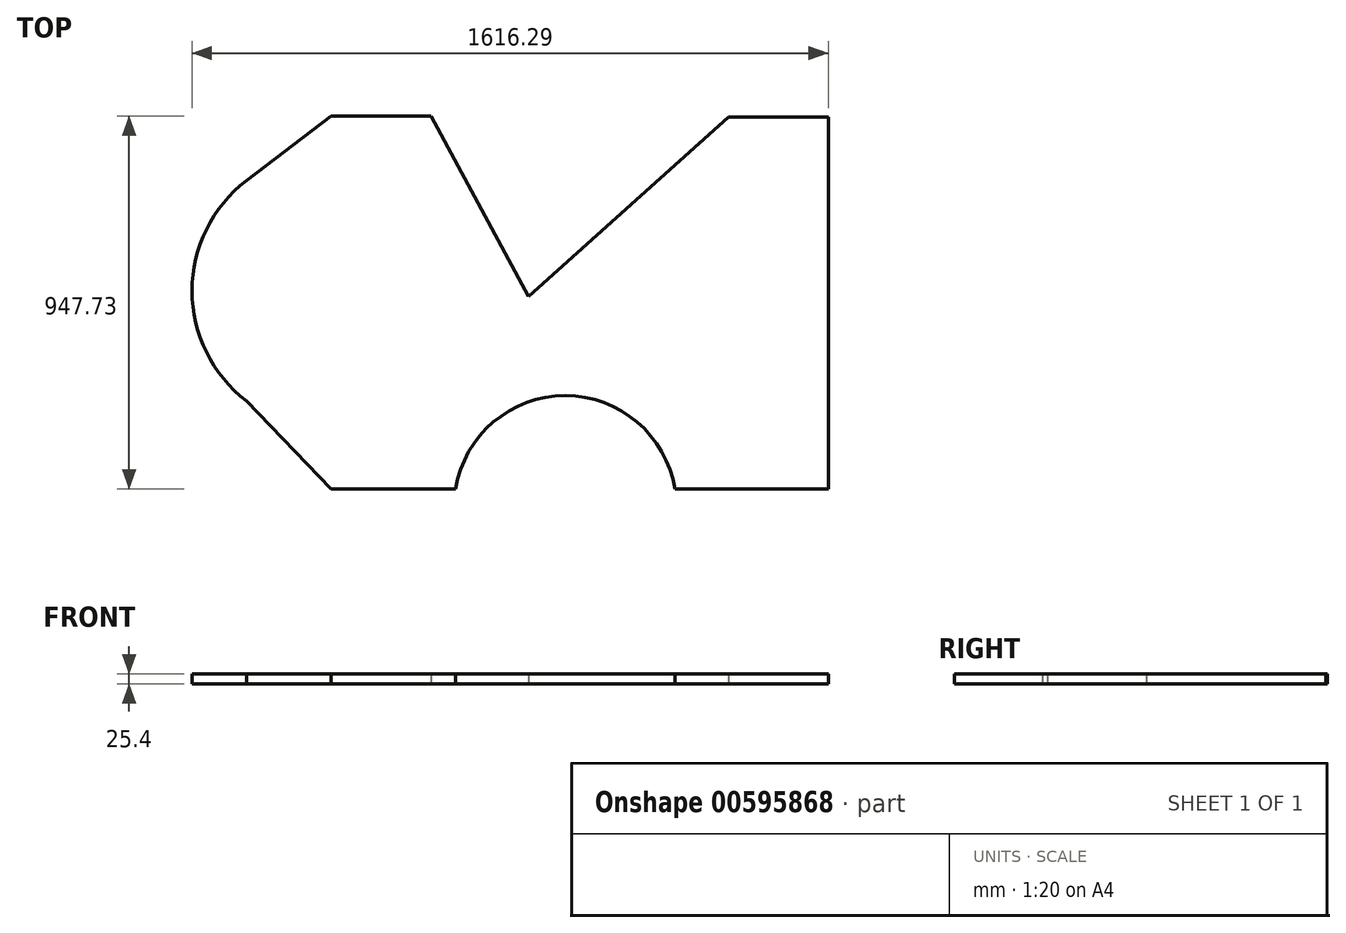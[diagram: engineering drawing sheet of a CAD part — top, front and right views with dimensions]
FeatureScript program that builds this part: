
annotation { "Feature Type Name" : "Feature", "Feature Type Description" : "" }
export const myFeature = defineFeature(function(context is Context, id is Id, definition is map)
    precondition{}
    {
        {
            var Q0;
            Q0=qCreatedBy(makeId("Top.planeOp"),FACE);
            var sketch = newSketch(context, id + "F0", { "sketchPlane" : qUnion([Q0])});
            skLineSegment(sketch, "E0", {"start": v(-501.68, 459.06) * mm, "end": v(-247.68, 459.06) * mm});
            skLineSegment(sketch, "E1", {"start": v(-247.68, 459.06) * mm, "end": v(0, 0) * mm});
            skLineSegment(sketch, "E2", {"start": v(0, 0) * mm, "end": v(508, 455.6) * mm});
            skLineSegment(sketch, "E3", {"start": v(508, 455.6) * mm, "end": v(762, 455.6) * mm});
            skLineSegment(sketch, "E4", {"start": v(762, 455.6) * mm, "end": v(762, -488.67) * mm});
            skLineSegment(sketch, "E5", {"start": v(762, -488.67) * mm, "end": v(372.3, -488.67) * mm});
            skArc(sketch, "E6", {"start": v(372.3, -488.67) * mm, "mid": v(93.72, -251.7) * mm, "end": v(-184.86, -488.67) * mm});
            skLineSegment(sketch, "E7", {"start": v(-184.86, -488.67) * mm, "end": v(-501.68, -488.67) * mm});
            skLineSegment(sketch, "E8", {"start": v(-716.09, -265.03) * mm, "end": v(-501.68, -488.67) * mm});
            skLineSegment(sketch, "E9", {"start": v(-501.68, 459.06) * mm, "end": v(-716.09, 294.83) * mm});
            skArc(sketch, "E10", {"start": v(-716.09, 294.83) * mm, "mid": v(-854.29, 14.9) * mm, "end": v(-716.09, -265.03) * mm});
            skLineSegment(sketch, "E11", {"start": v(-501.68, 459.06) * mm, "end": v(-501.68, -488.67) * mm, "construction": true});
            skSolve(sketch);
        }
        {
            var Q0;
            Q0=makeQuery(id+"F0.imprint","IMPRINT",FACE,{"disambiguationData":[TD([[makeQuery(id+"F0.imprint","IMPRINT",EDGE,{"derivedFrom":sQuery(id+"F0.wireOp",EDGE,"E0")}),-1.0]])]});
            extrude(context, id + "F1", {"entities" : qUnion([Q0]), "depth" : 25.4 * mm, "offsetDistance" : 25.4 * mm});
        }
    });
